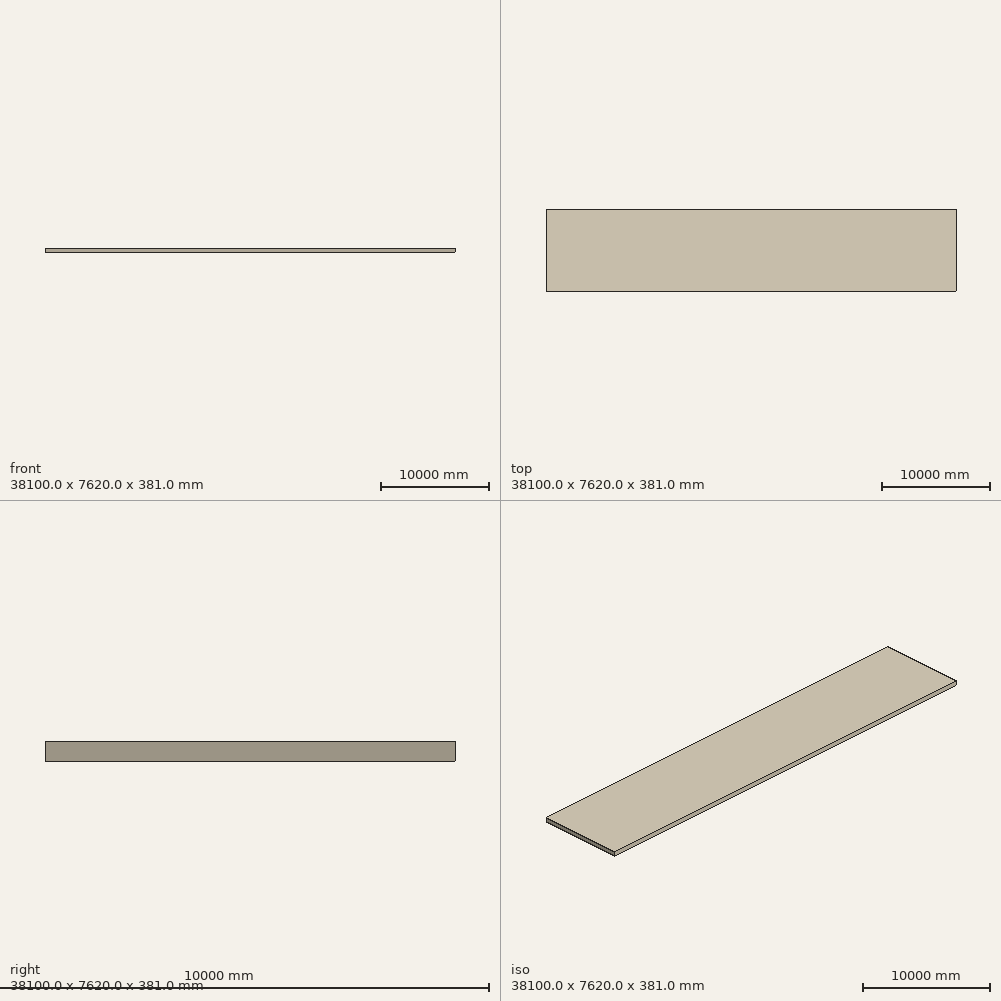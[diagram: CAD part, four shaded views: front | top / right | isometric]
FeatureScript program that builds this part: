
annotation { "Feature Type Name" : "Feature", "Feature Type Description" : "" }
export const myFeature = defineFeature(function(context is Context, id is Id, definition is map)
    precondition{}
    {
        {
            var Q0;
            Q0=qCreatedBy(makeId("Top.planeOp"),FACE);
            var sketch = newSketch(context, id + "F0", { "sketchPlane" : qUnion([Q0])});
            skLineSegment(sketch, "E0.bottom", {"start": v(-38056.54, 7522.67) * mm, "end": v(43.46, 7522.67) * mm});
            skLineSegment(sketch, "E0.top", {"start": v(-38056.54, -97.33) * mm, "end": v(43.46, -97.33) * mm});
            skLineSegment(sketch, "E0.left", {"start": v(-38056.54, 7522.67) * mm, "end": v(-38056.54, -97.33) * mm});
            skLineSegment(sketch, "E0.right", {"start": v(43.46, 7522.67) * mm, "end": v(43.46, -97.33) * mm});
            skSolve(sketch);
        }
        {
            var Q0;
            Q0=makeQuery(id+"F0.imprint","IMPRINT",FACE,{"disambiguationData":[TD([[makeQuery(id+"F0.imprint","IMPRINT",EDGE,{"derivedFrom":sQuery(id+"F0.wireOp",EDGE,"E0.bottom")}),-1.0]])]});
            extrude(context, id + "F1", {"entities" : qUnion([Q0]), "depth" : 381 * mm, "offsetDistance" : 25.4 * mm});
        }
    });
